# Revit family: PD2-EN types Avec hôte
name_source: partatom
category: Dispositifs d'éclairage
units: mm (PartAtom-declared; Revit-internal decimal feet)

## family parameters
Conserver l'orientation des annotations = Oui
Cote de connecteur circulaire = Utiliser le diamètre
Couper avec des vides une fois chargée = Non
Hôte = Face
Partagée = Non
Point de calcul de pièce = Non
Type d'élément = Normal

## types (12) — shared parameters
Classe = II
Code d'assemblage = D5010200
Fabricant = B.E.G.
Hauteur de montage max = 300 cm
IP = 20
Image du type = 360°.jpg
Marque = LUXOMAT
Mode de pose = Encastré
URL = http://www.luxomat.com
zero-valued in all types: Elévation par défaut

## per-type parameters (varying)
| type | Alimentation | Charge Cos ɸ =0.5 | Charge Cos ɸ =1 | Charge LED | Commentaires du type | Consommation | Modèle | Relais | Référence | Température ambiante | Type de Sortie |
| 01- PD2-EN Générique | 110-240 V AC |  |  |  | DET.PRES.360°/Ø10M ENCASTRE |  | PD2-EN |  |  | -25°C à +50°C |  |
| 05- PD2-S-EN réf 92156 | 110-240 V AC | 0 | 0 | 0 | DET.PRES.ESCLAVE..360°/Ø10M ENCASTRE | 0,25 W | PD2-S-EN | 10 A | 92156 | -25°C à +50°C | Esclave |
| 02- PD2-M-1C-EN réf 92555 | 110-240 V AC | 1150 VA | 2300 W | 300 W | DET.PRES.MAITRE.1 CONTACT.360°/Ø10M ENCASTRE | 0,47 W | PD2-M-1C-EN | 10 A | 92555 | -25°C à +50°C | TOR |
| 03- PD2-M-2C-EN réf 92155 | 110-240 V AC | 1150 VA | 2300 W | 300 W | DET.PRES.MAITRE.2 CONTACTS.360°/Ø10M ENCASTRE | 0,52 W | PD2-M-2C-EN | 10 A | 92155 | -25°C à +50°C | TOR |
| 04- PD2-DIM-EN réf 92157 | 110-240 V AC | 1150 VA | 2300 W | 300 W | DET.PRES.MAITRE.DIM(1-10V).360°/Ø10M ENCASTRE | 0,47 W | PD2-M-DIM-EN | 10 A | 92157 | -25°C à +50°C | DIM (50 ballasts maxi) |
| 10- PD2N-KNX-DX-EN réf 93361 | 24 V DC par Bus KNX | 0 | 0 | 0 | DET.PRES.KNX.VERSION DELUXE.360°/Ø10M ENCASTRE | 12 mA | PD2N-KNX-DX-EN | 0 | 93361 | -5°C à +45°C | KNX - 1 sortie Eclairage TOR ou GRADATION / 3 sorties Présence / Capteur de température et bruit |
| 08- PD2N-KNX-BA-EN réf 93381 | 24 V DC par Bus KNX | 0 | 0 | 0 | DET.PRES.KNX.VERSION BASIQUE.360°/Ø10M ENCASTRE | 12 mA | PD2N-KNX-BA-EN | 0 | 93381 | -5°C à +45°C | KNX - 1 sortie Eclairage TOR |
| 09- PD2N-KNX-ST-EN réf 93383 | 24 V DC par Bus KNX | 0 | 0 | 0 | DET.PRES.KNX.VERSION STANDARD.360°/Ø10M ENCASTRE | 12 mA | PD2N-KNX-ST-EN | 0 | 93383 | -5°C à +45°C | KNX - 1 sortie Eclairage TOR ou GRADATION / 3 sorties Présence |
| 06- PD2N-DALISYS-EN réf 93368 | 10-22 V DC par Bus DALI | 0 | 0 | 0 | MULTI.CAPTEUR.PRES.DALISYS.360°/Ø10M ENCASTRE | 3 mA | PD2N-DALISYS-EN | 0 | 93368 | -25°C à +55°C | DALI Adressable |
| 07- PD2N-BMS-DALI-2-EN réf 93544 | 10-22 V DC par Bus DALI | 0 | 0 | 0 | MULTI.CAPTEUR.PRES.BMS-DALI 2.360°/Ø10M ENCASTRE | 7 mA | PD2N-BMS-DALI-2-EN | 0 | 93544 | -25°C à +55°C | DALI 2 Adressable - BMS |
| 11- PD2N-KNXs-ST-EN réf 93511 | 24 V DC par Bus KNX | 0 | 0 | 0 | DET.PRES.KNX Sécure.VERSION STANDARD.360°/Ø10M ENCASTRE | 12 mA | PD2N-KNXs-ST-EN | 0 | 93511 | -5°C à +45°C | KNX Sécure- 1 sortie Eclairage TOR ou GRADATION / 3 sorties Présence / HCL |
| 12- PD2N-KNXs-DX-EN réf 93513 | 24 V DC par Bus KNX | 0 | 0 | 0 | DET.PRES.KNX Sécure.VERSION DELUXE.360°/Ø10M ENCASTRE | 12 mA | PD2N-KNXs-DX-EN | 0 | 93513 | -5°C à +45°C | KNX Sécure - 1 sortie Eclairage TOR ou GRADATION / 3 sorties Présence / Capteur de température et bruit / HCL |
